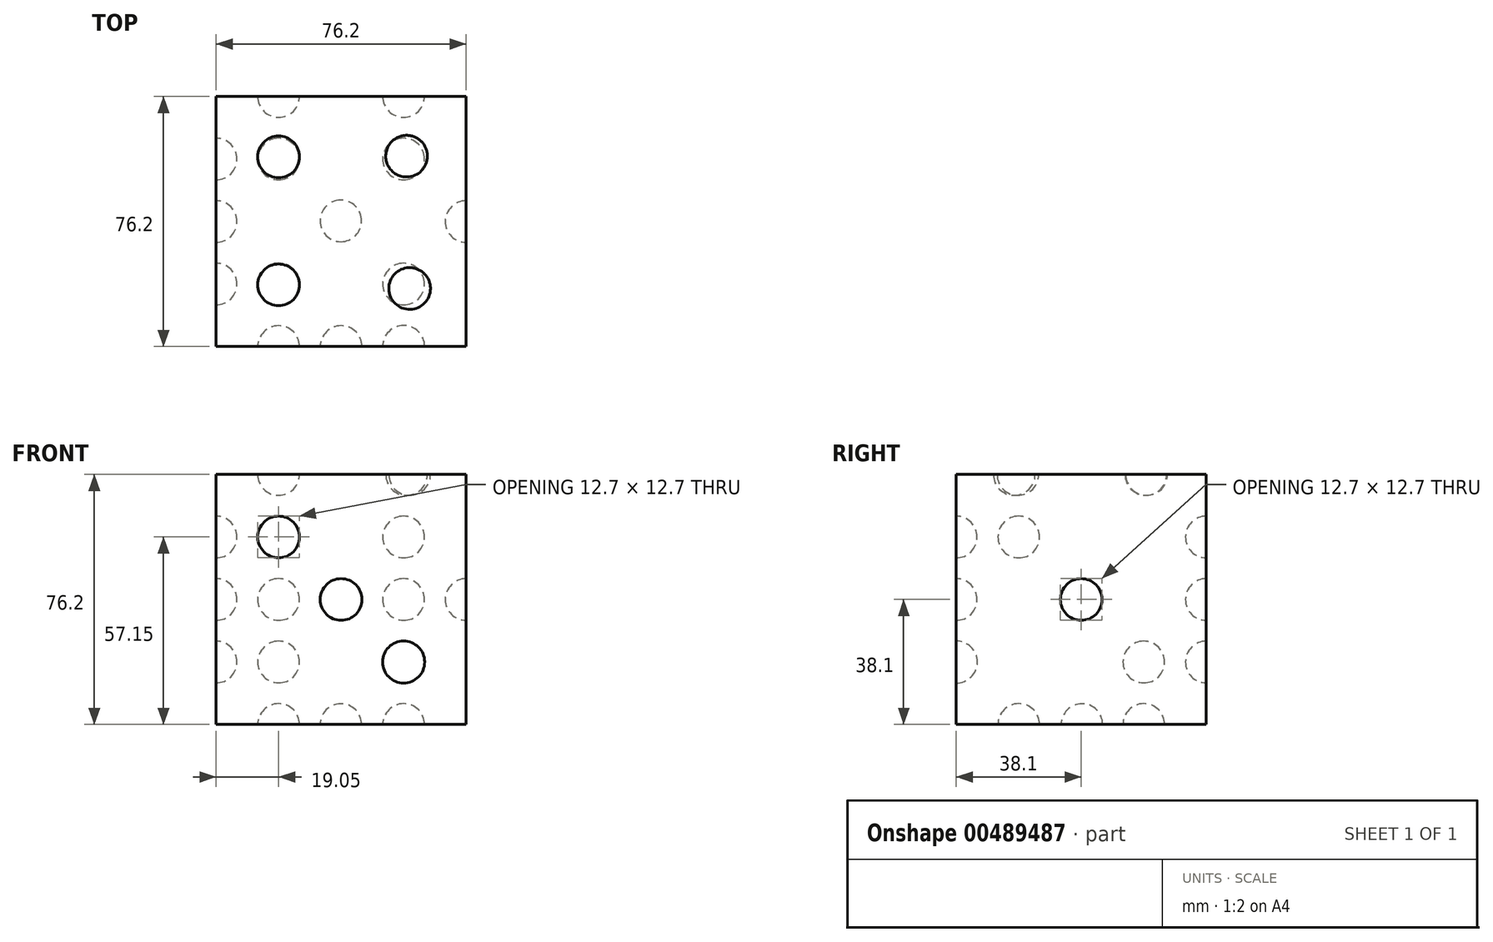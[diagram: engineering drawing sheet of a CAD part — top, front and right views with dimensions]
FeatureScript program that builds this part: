
annotation { "Feature Type Name" : "Feature", "Feature Type Description" : "" }
export const myFeature = defineFeature(function(context is Context, id is Id, definition is map)
    precondition{}
    {
        {
            var Q0;
            Q0=qCreatedBy(makeId("Front.planeOp"),FACE);
            var sketch = newSketch(context, id + "F0", { "sketchPlane" : qUnion([Q0])});
            skLineSegment(sketch, "E0.bottom", {"start": v(0, 76.2) * mm, "end": v(76.2, 76.2) * mm});
            skLineSegment(sketch, "E0.top", {"start": v(0, 0) * mm, "end": v(76.2, 0) * mm});
            skLineSegment(sketch, "E0.left", {"start": v(0, 76.2) * mm, "end": v(0, 0) * mm});
            skLineSegment(sketch, "E0.right", {"start": v(76.2, 76.2) * mm, "end": v(76.2, 0) * mm});
            skSolve(sketch);
        }
        {
            var Q0;
            Q0=makeQuery(id+"F0.imprint","IMPRINT",FACE,{"disambiguationData":[TD([[makeQuery(id+"F0.imprint","IMPRINT",EDGE,{"derivedFrom":sQuery(id+"F0.wireOp",EDGE,"E0.bottom")}),-1.0]])]});
            extrude(context, id + "F1", {"entities" : qUnion([Q0]), "depth" : 76.2 * mm});
        }
        {
            var Q0;
            Q0=makeQuery(id+"F1.opExtrude","SWEPT_FACE",FACE,{"disambiguationData":[OSD([sQuery(id+"F0.wireOp",EDGE,"E0.right")])]});
            var sketch = newSketch(context, id + "F2", { "sketchPlane" : qUnion([Q0])});
            skArc(sketch, "E1", {"start": v(-38.1, 44.45) * mm, "mid": v(-44.45, 38.1) * mm, "end": v(-38.1, 31.75) * mm});
            skLineSegment(sketch, "E2", {"start": v(-38.1, 38.1) * mm, "end": v(-38.1, 44.45) * mm});
            skPoint(sketch, "E3.orphan", {"position": v(-76.2, 0) * mm});
            skPoint(sketch, "E4.orphan", {"position": v(0, 76.2) * mm});
            skPoint(sketch, "E5.end.orphan", {"position": v(-38.1, 0) * mm});
            skPoint(sketch, "E6.orphan", {"position": v(-38.1, 76.2) * mm});
            skLineSegment(sketch, "E7", {"start": v(-38.1, 76.2) * mm, "end": v(-38.1, 0) * mm});
            skSolve(sketch);
        }
        {
            var Q0;
            {var subQ0=sQuery(id+"F2.wireOp",EDGE,"E1");Q0=makeQuery(id+"F2.imprint","IMPRINT",FACE,{"disambiguationData":[TD([[makeQuery(id+"F2.imprint","IMPRINT",EDGE,{"derivedFrom":subQ0}),1.0]])]});}
            var Q1;
            Q1=sQuery(id+"F2.wireOp",EDGE,"E7");
            revolve(context, id + "F3", {"operationType" : NewBodyOperationType.REMOVE, "entities" : qUnion([Q0]), "axis" : qUnion([Q1]), "revolveType" : RevolveType.FULL, "oppositeDirection" : true});
        }
        {
            var Q0;
            Q0=qCreatedBy(makeId("Top.planeOp"),FACE);
            var sketch = newSketch(context, id + "F4", { "sketchPlane" : qUnion([Q0])});
            skArc(sketch, "E8", {"start": v(38.01, -31.57) * mm, "mid": v(31.68, -37.9) * mm, "end": v(38.01, -44.23) * mm});
            skPoint(sketch, "E9.orphan", {"position": v(0, 0) * mm});
            skPoint(sketch, "E10.start.orphan", {"position": v(76.02, 0) * mm});
            skPoint(sketch, "E11.trimOffspring.end.orphan", {"position": v(0, -75.8) * mm});
            skPoint(sketch, "E12.end.orphan", {"position": v(76.02, -75.8) * mm});
            skLineSegment(sketch, "E13", {"start": v(38.01, -37.9) * mm, "end": v(38.01, 0) * mm});
            skLineSegment(sketch, "E14", {"start": v(38.01, -37.9) * mm, "end": v(38.01, -76.25) * mm});
            skLineSegment(sketch, "E15", {"start": v(38.01, 0) * mm, "end": v(38.01, -66.48) * mm});
            skLineSegment(sketch, "E16", {"start": v(38.01, -66.48) * mm, "end": v(38.01, 0) * mm});
            skSolve(sketch);
        }
        {
            var Q0;
            Q0 = qSketchRegion(id + "F4", true);
            var Q1;
            Q1=sQuery(id+"F4.wireOp",EDGE,"E16");
            revolve(context, id + "F5", {"operationType" : NewBodyOperationType.REMOVE, "entities" : qUnion([Q0]), "axis" : qUnion([Q1]), "revolveType" : RevolveType.FULL});
        }
        {
            var Q0;
            Q0=makeQuery(id+"F1.opExtrude","SWEPT_FACE",FACE,{"disambiguationData":[OSD([sQuery(id+"F0.wireOp",EDGE,"E0.bottom")])]});
            var sketch = newSketch(context, id + "F6", { "sketchPlane" : qUnion([Q0])});
            skSolve(sketch);
        }
        {
            var Q0;
            Q0=makeQuery(id+"F1.opExtrude","SWEPT_FACE",FACE,{"disambiguationData":[OSD([sQuery(id+"F0.wireOp",EDGE,"E0.top")])]});
            var sketch = newSketch(context, id + "F7", { "sketchPlane" : qUnion([Q0])});
            skArc(sketch, "E17", {"start": v(33.6, 33.6) * mm, "mid": v(43.97, 40.53) * mm, "end": v(31.75, 38.1) * mm});
            skPoint(sketch, "E18.orphan", {"position": v(38.1, 76.2) * mm});
            skPoint(sketch, "E19.orphan", {"position": v(38.1, 0) * mm});
            skLineSegment(sketch, "E20", {"start": v(19.05, 76.2) * mm, "end": v(19.05, 0) * mm});
            skPoint(sketch, "E20.startSnap0", {"position": v(19.05, 57.15) * mm});
            skPoint(sketch, "E21.startSnap0", {"position": v(57.15, 57.15) * mm});
            skPoint(sketch, "E22.orphan", {"position": v(0, 38.1) * mm});
            skPoint(sketch, "E23.end.orphan", {"position": v(76.2, 38.1) * mm});
            skArc(sketch, "E24", {"start": v(19.05, 63.5) * mm, "mid": v(12.7, 57.15) * mm, "end": v(19.05, 50.8) * mm});
            skArc(sketch, "E25", {"start": v(57.15, 63.5) * mm, "mid": v(50.8, 57.15) * mm, "end": v(57.15, 50.8) * mm});
            skPoint(sketch, "E26.orphan", {"position": v(57.15, 0) * mm});
            skPoint(sketch, "E21.start.orphan", {"position": v(57.15, 76.2) * mm});
            skSolve(sketch);
        }
        {
            var Q0;
            {var subQ1=sQuery(id+"F0.wireOp",EDGE,"E0.top");var subQ6=makeQuery(id+"F1.opExtrude","SWEPT_EDGE",EDGE,{"disambiguationData":[OSD([subQ1,sQuery(id+"F0.wireOp",EDGE,"E0.right")])]});Q0=makeQuery(id+"F7.imprint","IMPRINT",FACE,{"disambiguationData":[TD([[makeQuery(id+"F7.imprint","IMPRINT",EDGE,{"derivedFrom":subQ6}),-1.0]])]});}
            var sketch = newSketch(context, id + "F8", { "sketchPlane" : qUnion([Q0])});
            skSolve(sketch);
        }
        {
            var Q0;
            Q0 = qSketchRegion(id + "F7", true);
            var Q1;
            Q1=sQuery(id+"F7.wireOp",EDGE,"E20");
            revolve(context, id + "F9", {"operationType" : NewBodyOperationType.REMOVE, "entities" : qUnion([Q0]), "axis" : qUnion([Q1]), "revolveType" : RevolveType.FULL, "oppositeDirection" : true});
        }
        {
            var Q0;
            Q0=makeQuery(id+"F1.opExtrude","SWEPT_FACE",FACE,{"disambiguationData":[OSD([sQuery(id+"F0.wireOp",EDGE,"E0.top")])]});
            var sketch = newSketch(context, id + "F10", { "sketchPlane" : qUnion([Q0])});
            skLineSegment(sketch, "E27", {"start": v(57.15, 76.2) * mm, "end": v(57.15, 0) * mm});
            skPoint(sketch, "E27.startSnap0", {"position": v(57.15, 57.15) * mm});
            skPoint(sketch, "E28.orphan", {"position": v(38.1, 76.2) * mm});
            skPoint(sketch, "E29.end.orphan", {"position": v(76.2, 38.1) * mm});
            skArc(sketch, "E30", {"start": v(57.15, 63.5) * mm, "mid": v(50.8, 57.15) * mm, "end": v(57.15, 50.8) * mm});
            skSolve(sketch);
        }
        {
            var Q0;
            Q0 = qSketchRegion(id + "F10", true);
            var Q1;
            Q1=sQuery(id+"F10.wireOp",EDGE,"E27");
            revolve(context, id + "F11", {"operationType" : NewBodyOperationType.REMOVE, "entities" : qUnion([Q0]), "axis" : qUnion([Q1]), "revolveType" : RevolveType.FULL, "oppositeDirection" : true});
        }
        {
            var Q0;
            Q0=makeQuery(id+"F1.opExtrude","SWEPT_FACE",FACE,{"disambiguationData":[OSD([sQuery(id+"F0.wireOp",EDGE,"E0.top")])]});
            var sketch = newSketch(context, id + "F12", { "sketchPlane" : qUnion([Q0])});
            skLineSegment(sketch, "E31", {"start": v(57.15, 57.15) * mm, "end": v(57.15, 0) * mm});
            skArc(sketch, "E32", {"start": v(57.15, 25.4) * mm, "mid": v(50.8, 19.05) * mm, "end": v(57.15, 12.7) * mm});
            skPoint(sketch, "E33.orphan", {"position": v(76.2, 38.1) * mm});
            skPoint(sketch, "E34.orphan", {"position": v(38.1, 0) * mm});
            skSolve(sketch);
        }
        {
            var Q0;
            Q0 = qSketchRegion(id + "F12", true);
            var Q1;
            Q1=sQuery(id+"F12.wireOp",EDGE,"E31");
            revolve(context, id + "F13", {"operationType" : NewBodyOperationType.REMOVE, "entities" : qUnion([Q0]), "axis" : qUnion([Q1]), "revolveType" : RevolveType.FULL, "oppositeDirection" : true});
        }
        {
            var Q0;
            Q0=makeQuery(id+"F1.opExtrude","SWEPT_FACE",FACE,{"disambiguationData":[OSD([sQuery(id+"F0.wireOp",EDGE,"E0.top")])]});
            var sketch = newSketch(context, id + "F14", { "sketchPlane" : qUnion([Q0])});
            skLineSegment(sketch, "E35", {"start": v(19.05, 57.15) * mm, "end": v(19.05, 0) * mm});
            skArc(sketch, "E36", {"start": v(19.05, 25.4) * mm, "mid": v(12.7, 19.05) * mm, "end": v(19.05, 12.7) * mm});
            skPoint(sketch, "E36.perimeterSnap0", {"position": v(19.05, 19.05) * mm});
            skPoint(sketch, "E37.orphan", {"position": v(0, 38.1) * mm});
            skPoint(sketch, "E38.orphan", {"position": v(38.1, 0) * mm});
            skSolve(sketch);
        }
        {
            var Q0;
            Q0 = qSketchRegion(id + "F14", true);
            var Q1;
            Q1=sQuery(id+"F14.wireOp",EDGE,"E35");
            revolve(context, id + "F15", {"operationType" : NewBodyOperationType.REMOVE, "entities" : qUnion([Q0]), "axis" : qUnion([Q1]), "revolveType" : RevolveType.FULL, "oppositeDirection" : true});
        }
        {
            var Q0;
            Q0=makeQuery(id+"F1.opExtrude","CAP_FACE",FACE,{"disambiguationData":[OSD([sQuery(id+"F0.wireOp",EDGE,"E0.bottom"),sQuery(id+"F0.wireOp",EDGE,"E0.top"),sQuery(id+"F0.wireOp",EDGE,"E0.left"),sQuery(id+"F0.wireOp",EDGE,"E0.right")])],"isStart":false});
            var sketch = newSketch(context, id + "F16", { "sketchPlane" : qUnion([Q0])});
            skArc(sketch, "E39", {"start": v(19.05, 63.5) * mm, "mid": v(12.7, 57.15) * mm, "end": v(19.05, 50.8) * mm});
            skArc(sketch, "E40", {"start": v(38.1, 44.45) * mm, "mid": v(31.75, 38.1) * mm, "end": v(38.1, 31.75) * mm});
            skArc(sketch, "E41", {"start": v(57.15, 25.4) * mm, "mid": v(50.8, 19.05) * mm, "end": v(57.15, 12.7) * mm});
            skLineSegment(sketch, "E42", {"start": v(19.05, 76.2) * mm, "end": v(19.05, 0) * mm});
            skPoint(sketch, "E43.orphan", {"position": v(0, 38.1) * mm});
            skPoint(sketch, "E44.start.orphan", {"position": v(0, 0) * mm});
            skPoint(sketch, "E45.trimOffspring.end.orphan", {"position": v(76.2, 76.2) * mm});
            skPoint(sketch, "E46.orphan", {"position": v(76.2, 38.1) * mm});
            skPoint(sketch, "E47.orphan", {"position": v(38.1, 0) * mm});
            skPoint(sketch, "E48.orphan", {"position": v(38.1, 76.2) * mm});
            skPoint(sketch, "E49.orphan", {"position": v(57.15, 76.2) * mm});
            skPoint(sketch, "E50.end.orphan", {"position": v(57.15, 0) * mm});
            skSolve(sketch);
        }
        {
            var Q0;
            Q0 = qSketchRegion(id + "F16", true);
            var Q1;
            Q1=sQuery(id+"F16.wireOp",EDGE,"E42");
            revolve(context, id + "F17", {"operationType" : NewBodyOperationType.REMOVE, "entities" : qUnion([Q0]), "axis" : qUnion([Q1]), "revolveType" : RevolveType.FULL, "oppositeDirection" : true});
        }
        {
            var Q0;
            Q0=makeQuery(id+"F1.opExtrude","CAP_FACE",FACE,{"disambiguationData":[OSD([sQuery(id+"F0.wireOp",EDGE,"E0.bottom"),sQuery(id+"F0.wireOp",EDGE,"E0.top"),sQuery(id+"F0.wireOp",EDGE,"E0.left"),sQuery(id+"F0.wireOp",EDGE,"E0.right")])],"isStart":false});
            var sketch = newSketch(context, id + "F18", { "sketchPlane" : qUnion([Q0])});
            skPoint(sketch, "E51.startSnap0", {"position": v(57.15, 57.15) * mm});
            skPoint(sketch, "E52.orphan", {"position": v(38.1, 76.2) * mm});
            skPoint(sketch, "E53.orphan", {"position": v(76.2, 38.1) * mm});
            skPoint(sketch, "E51.start.orphan", {"position": v(57.15, 76.2) * mm});
            skLineSegment(sketch, "E54", {"start": v(38.1, 76.2) * mm, "end": v(38.1, 0) * mm});
            skArc(sketch, "E55", {"start": v(38.1, 44.45) * mm, "mid": v(31.75, 38.1) * mm, "end": v(38.1, 31.75) * mm});
            skPoint(sketch, "E56.orphan", {"position": v(0, 38.1) * mm});
            skSolve(sketch);
        }
        {
            var Q0;
            Q0 = qSketchRegion(id + "F18", true);
            var Q1;
            Q1=sQuery(id+"F18.wireOp",EDGE,"E54");
            revolve(context, id + "F19", {"operationType" : NewBodyOperationType.REMOVE, "entities" : qUnion([Q0]), "axis" : qUnion([Q1]), "revolveType" : RevolveType.FULL, "oppositeDirection" : true});
        }
        {
            var Q0;
            Q0=makeQuery(id+"F1.opExtrude","CAP_FACE",FACE,{"disambiguationData":[OSD([sQuery(id+"F0.wireOp",EDGE,"E0.bottom"),sQuery(id+"F0.wireOp",EDGE,"E0.top"),sQuery(id+"F0.wireOp",EDGE,"E0.left"),sQuery(id+"F0.wireOp",EDGE,"E0.right")])],"isStart":false});
            var sketch = newSketch(context, id + "F20", { "sketchPlane" : qUnion([Q0])});
            skLineSegment(sketch, "E57", {"start": v(57.15, 0) * mm, "end": v(57.15, 76.2) * mm});
            skPoint(sketch, "E57.startSnap0", {"position": v(57.15, 19.05) * mm});
            skArc(sketch, "E58", {"start": v(57.15, 25.46) * mm, "mid": v(50.74, 19.05) * mm, "end": v(57.15, 12.64) * mm});
            skPoint(sketch, "E59.orphan", {"position": v(76.2, 38.1) * mm});
            skPoint(sketch, "E60.orphan", {"position": v(38.1, 0) * mm});
            skSolve(sketch);
        }
        {
            var Q0;
            Q0 = qSketchRegion(id + "F20", true);
            var Q1;
            Q1=sQuery(id+"F20.wireOp",EDGE,"E57");
            revolve(context, id + "F21", {"operationType" : NewBodyOperationType.REMOVE, "entities" : qUnion([Q0]), "axis" : qUnion([Q1]), "revolveType" : RevolveType.FULL, "oppositeDirection" : true});
        }
        {
            var Q0;
            {var subQ0=sQuery(id+"F0.wireOp",EDGE,"E0.bottom");Q0=makeQuery(id+"F6.imprint","IMPRINT",FACE,{"disambiguationData":[TD([[makeQuery(id+"F6.imprint","IMPRINT",EDGE,{"derivedFrom":makeQuery(id+"F1.opExtrude","CAP_EDGE",EDGE,{"disambiguationData":[OSD([subQ0])],"isStart":true})}),-1.0]])]});}
            var sketch = newSketch(context, id + "F22", { "sketchPlane" : qUnion([Q0])});
            skLineSegment(sketch, "E61", {"start": v(0, 0) * mm, "end": v(38.1, 0) * mm});
            skLineSegment(sketch, "E62", {"start": v(19.05, 0) * mm, "end": v(19.05, -76.9) * mm});
            skArc(sketch, "E63", {"start": v(19.05, -12.05) * mm, "mid": v(12.7, -18.4) * mm, "end": v(19.05, -24.75) * mm});
            skArc(sketch, "E64", {"start": v(19.05, -51.05) * mm, "mid": v(12.7, -57.4) * mm, "end": v(19.05, -63.75) * mm});
            skLineSegment(sketch, "E65", {"start": v(38.1, 0) * mm, "end": v(75.8, 0) * mm});
            skLineSegment(sketch, "E66", {"start": v(56.95, 0) * mm, "end": v(56.95, -76.46) * mm});
            skPoint(sketch, "E67.start.orphan", {"position": v(0, -39) * mm});
            skSolve(sketch);
        }
        {
            var Q0;
            Q0 = qSketchRegion(id + "F22", true);
            var Q1;
            Q1=sQuery(id+"F22.wireOp",EDGE,"E62");
            revolve(context, id + "F23", {"operationType" : NewBodyOperationType.REMOVE, "entities" : qUnion([Q0]), "axis" : qUnion([Q1]), "revolveType" : RevolveType.FULL, "oppositeDirection" : true});
        }
        {
            var Q0;
            {var subQ0=sQuery(id+"F0.wireOp",EDGE,"E0.bottom");Q0=makeQuery(id+"F6.imprint","IMPRINT",FACE,{"disambiguationData":[TD([[makeQuery(id+"F6.imprint","IMPRINT",EDGE,{"derivedFrom":makeQuery(id+"F1.opExtrude","CAP_EDGE",EDGE,{"disambiguationData":[OSD([subQ0])],"isStart":true})}),-1.0]])]});}
            var sketch = newSketch(context, id + "F24", { "sketchPlane" : qUnion([Q0])});
            skLineSegment(sketch, "E68", {"start": v(0, 0) * mm, "end": v(38.12, 0) * mm});
            skLineSegment(sketch, "E69", {"start": v(57.62, 0) * mm, "end": v(59.4, -76.69) * mm});
            skArc(sketch, "E70", {"start": v(57.9, -11.83) * mm, "mid": v(51.7, -18.32) * mm, "end": v(58.2, -24.52) * mm});
            skArc(sketch, "E71", {"start": v(58.83, -52.16) * mm, "mid": v(52.63, -58.66) * mm, "end": v(59.12, -64.86) * mm});
            skPoint(sketch, "E72.orphan", {"position": v(0, -18.17) * mm});
            skPoint(sketch, "E73.end.orphan", {"position": v(39.9, -76.69) * mm});
            skPoint(sketch, "E74.orphan", {"position": v(0, -58.51) * mm});
            skPoint(sketch, "E75.end.orphan", {"position": v(76.24, -58.51) * mm});
            skPoint(sketch, "E76.orphan", {"position": v(76.24, -18.17) * mm});
            skSolve(sketch);
        }
        {
            var Q0;
            Q0 = qSketchRegion(id + "F24", true);
            var Q1;
            Q1=sQuery(id+"F24.wireOp",EDGE,"E69");
            revolve(context, id + "F25", {"operationType" : NewBodyOperationType.REMOVE, "entities" : qUnion([Q0]), "axis" : qUnion([Q1]), "revolveType" : RevolveType.FULL, "oppositeDirection" : true});
        }
        {
            var Q0;
            Q0=makeQuery(id+"F1.opExtrude","CAP_FACE",FACE,{"disambiguationData":[OSD([sQuery(id+"F0.wireOp",EDGE,"E0.bottom"),sQuery(id+"F0.wireOp",EDGE,"E0.top"),sQuery(id+"F0.wireOp",EDGE,"E0.left"),sQuery(id+"F0.wireOp",EDGE,"E0.right")])],"isStart":true});
            var sketch = newSketch(context, id + "F26", { "sketchPlane" : qUnion([Q0])});
            skLineSegment(sketch, "E77", {"start": v(-76.2, 76.2) * mm, "end": v(-38.1, 76.2) * mm});
            skLineSegment(sketch, "E78", {"start": v(-57.15, 76.2) * mm, "end": v(-57.15, 0) * mm});
            skLineSegment(sketch, "E79", {"start": v(-38.1, 76.2) * mm, "end": v(0, 76.2) * mm});
            skArc(sketch, "E80", {"start": v(-57.15, 63.5) * mm, "mid": v(-63.5, 57.15) * mm, "end": v(-57.15, 50.8) * mm});
            skArc(sketch, "E81", {"start": v(-57.15, 44.45) * mm, "mid": v(-63.5, 38.1) * mm, "end": v(-57.15, 31.75) * mm});
            skArc(sketch, "E82", {"start": v(-57.15, 25.4) * mm, "mid": v(-63.5, 19.05) * mm, "end": v(-57.15, 12.7) * mm});
            skArc(sketch, "E83", {"start": v(-19.05, 63.5) * mm, "mid": v(-25.4, 57.15) * mm, "end": v(-19.05, 50.8) * mm});
            skArc(sketch, "E84", {"start": v(-19.05, 25.4) * mm, "mid": v(-25.4, 19.05) * mm, "end": v(-19.05, 12.7) * mm});
            skPoint(sketch, "E85.orphan", {"position": v(-76.2, 38.1) * mm});
            skPoint(sketch, "E86.orphan", {"position": v(0, 38.1) * mm});
            skPoint(sketch, "E87.orphan", {"position": v(-38.1, 0) * mm});
            skPoint(sketch, "E88.trimOffspring.end.orphan", {"position": v(-19.05, 38.1) * mm});
            skArc(sketch, "E89", {"start": v(-19.05, 44.45) * mm, "mid": v(-25.4, 38.1) * mm, "end": v(-19.05, 31.75) * mm});
            skPoint(sketch, "E90.orphan", {"position": v(-19.05, 76.2) * mm});
            skPoint(sketch, "E91.orphan", {"position": v(-19.05, 0) * mm});
            skSolve(sketch);
        }
        {
            var Q0;
            Q0 = qSketchRegion(id + "F26", true);
            var Q1;
            Q1=sQuery(id+"F26.wireOp",EDGE,"E78");
            revolve(context, id + "F27", {"operationType" : NewBodyOperationType.REMOVE, "entities" : qUnion([Q0]), "axis" : qUnion([Q1]), "revolveType" : RevolveType.FULL});
        }
        {
            var Q0;
            Q0=makeQuery(id+"F1.opExtrude","CAP_FACE",FACE,{"disambiguationData":[OSD([sQuery(id+"F0.wireOp",EDGE,"E0.bottom"),sQuery(id+"F0.wireOp",EDGE,"E0.top"),sQuery(id+"F0.wireOp",EDGE,"E0.left"),sQuery(id+"F0.wireOp",EDGE,"E0.right")])],"isStart":true});
            var sketch = newSketch(context, id + "F28", { "sketchPlane" : qUnion([Q0])});
            skLineSegment(sketch, "E92", {"start": v(-19.05, 76.2) * mm, "end": v(-19.05, 0) * mm});
            skPoint(sketch, "E92.startSnap0", {"position": v(-19.05, 57.15) * mm});
            skArc(sketch, "E93", {"start": v(-19.05, 63.5) * mm, "mid": v(-25.4, 57.15) * mm, "end": v(-19.05, 50.8) * mm});
            skArc(sketch, "E94", {"start": v(-19.05, 44.45) * mm, "mid": v(-25.4, 38.1) * mm, "end": v(-19.05, 31.75) * mm});
            skArc(sketch, "E95", {"start": v(-19.05, 25.4) * mm, "mid": v(-25.4, 19.05) * mm, "end": v(-19.05, 12.7) * mm});
            skPoint(sketch, "E96.orphan", {"position": v(-38.1, 38.1) * mm});
            skPoint(sketch, "E97.start.orphan", {"position": v(-38.1, 76.2) * mm});
            skPoint(sketch, "E98.orphan", {"position": v(0, 38.1) * mm});
            skPoint(sketch, "E99.end.orphan", {"position": v(-38.1, 0) * mm});
            skSolve(sketch);
        }
        {
            var Q0;
            Q0 = qSketchRegion(id + "F28", true);
            var Q1;
            Q1=sQuery(id+"F28.wireOp",EDGE,"E92");
            revolve(context, id + "F29", {"operationType" : NewBodyOperationType.REMOVE, "entities" : qUnion([Q0]), "axis" : qUnion([Q1]), "revolveType" : RevolveType.FULL, "oppositeDirection" : true});
        }
        {
            var Q0;
            Q0=makeQuery(id+"F1.opExtrude","SWEPT_FACE",FACE,{"disambiguationData":[OSD([sQuery(id+"F0.wireOp",EDGE,"E0.left")])]});
            var sketch = newSketch(context, id + "F30", { "sketchPlane" : qUnion([Q0])});
            skLineSegment(sketch, "E100", {"start": v(38.1, 44.45) * mm, "end": v(38.1, 38.1) * mm});
            skLineSegment(sketch, "E101", {"start": v(19.05, 19.05) * mm, "end": v(19.05, 25.4) * mm});
            skPoint(sketch, "E101.startSnap0", {"position": v(19.05, 19.05) * mm});
            skLineSegment(sketch, "E102", {"start": v(57.15, 63.5) * mm, "end": v(57.15, 57.15) * mm});
            skPoint(sketch, "E102.startSnap0", {"position": v(57.15, 57.15) * mm});
            skArc(sketch, "E103", {"start": v(19.05, 25.4) * mm, "mid": v(12.7, 19.05) * mm, "end": v(19.05, 12.7) * mm});
            skArc(sketch, "E104", {"start": v(38.1, 44.45) * mm, "mid": v(31.75, 38.1) * mm, "end": v(38.1, 31.75) * mm});
            skArc(sketch, "E105", {"start": v(57.15, 63.5) * mm, "mid": v(50.8, 57.15) * mm, "end": v(57.15, 50.8) * mm});
            skPoint(sketch, "E106.orphan", {"position": v(0, 0) * mm});
            skPoint(sketch, "E107.orphan", {"position": v(76.2, 76.2) * mm});
            skPoint(sketch, "E108.orphan", {"position": v(38.1, 76.2) * mm});
            skPoint(sketch, "E109.orphan", {"position": v(57.15, 76.2) * mm});
            skLineSegment(sketch, "E110.trimOffspring", {"start": v(38.1, 31.75) * mm, "end": v(38.1, 0) * mm});
            skLineSegment(sketch, "E111.trimOffspring", {"start": v(57.15, 50.8) * mm, "end": v(57.15, 0) * mm});
            skPoint(sketch, "E112.orphan", {"position": v(19.05, 0) * mm});
            skLineSegment(sketch, "E113", {"start": v(38.1, 31.75) * mm, "end": v(38.1, 76.2) * mm});
            skLineSegment(sketch, "E114", {"start": v(57.15, 57.15) * mm, "end": v(57.15, 76.2) * mm});
            skSolve(sketch);
        }
        {
            var Q0;
            Q0 = qSketchRegion(id + "F30", true);
            var Q1;
            Q1=sQuery(id+"F30.wireOp",EDGE,"E113");
            revolve(context, id + "F31", {"operationType" : NewBodyOperationType.REMOVE, "entities" : qUnion([Q0]), "axis" : qUnion([Q1]), "revolveType" : RevolveType.FULL, "oppositeDirection" : true});
        }
        {
            var Q0;
            Q0=makeQuery(id+"F1.opExtrude","SWEPT_FACE",FACE,{"disambiguationData":[OSD([sQuery(id+"F0.wireOp",EDGE,"E0.left")])]});
            var sketch = newSketch(context, id + "F32", { "sketchPlane" : qUnion([Q0])});
            skLineSegment(sketch, "E115", {"start": v(19.05, 0) * mm, "end": v(19.05, 76.2) * mm});
            skPoint(sketch, "E115.startSnap0", {"position": v(19.05, 19.05) * mm});
            skLineSegment(sketch, "E116", {"start": v(38.1, 76.2) * mm, "end": v(76.2, 38.1) * mm});
            skLineSegment(sketch, "E117", {"start": v(57.15, 76.2) * mm, "end": v(57.15, 0) * mm});
            skPoint(sketch, "E117.startSnap0", {"position": v(57.15, 57.15) * mm});
            skArc(sketch, "E118", {"start": v(19.05, 25.4) * mm, "mid": v(12.7, 19.05) * mm, "end": v(19.05, 12.7) * mm});
            skPoint(sketch, "E119.orphan", {"position": v(0, 38.1) * mm});
            skPoint(sketch, "E120.end.orphan", {"position": v(38.1, 0) * mm});
            skSolve(sketch);
        }
        {
            var Q0;
            Q0 = qSketchRegion(id + "F32", true);
            var Q1;
            Q1=sQuery(id+"F32.wireOp",EDGE,"E115");
            revolve(context, id + "F33", {"operationType" : NewBodyOperationType.REMOVE, "entities" : qUnion([Q0]), "axis" : qUnion([Q1]), "revolveType" : RevolveType.FULL, "oppositeDirection" : true});
        }
        {
            var Q0;
            Q0=makeQuery(id+"F1.opExtrude","SWEPT_FACE",FACE,{"disambiguationData":[OSD([sQuery(id+"F0.wireOp",EDGE,"E0.left")])]});
            var sketch = newSketch(context, id + "F34", { "sketchPlane" : qUnion([Q0])});
            skLineSegment(sketch, "E121", {"start": v(57.15, 76.2) * mm, "end": v(57.15, 0) * mm});
            skPoint(sketch, "E121.startSnap0", {"position": v(57.15, 57.15) * mm});
            skArc(sketch, "E122", {"start": v(57.15, 63.5) * mm, "mid": v(50.8, 57.15) * mm, "end": v(57.15, 50.8) * mm});
            skPoint(sketch, "E123.orphan", {"position": v(38.1, 76.2) * mm});
            skPoint(sketch, "E124.orphan", {"position": v(76.2, 38.1) * mm});
            skSolve(sketch);
        }
        {
            var Q0;
            Q0 = qSketchRegion(id + "F34", true);
            var Q1;
            Q1=sQuery(id+"F34.wireOp",EDGE,"E121");
            revolve(context, id + "F35", {"operationType" : NewBodyOperationType.REMOVE, "entities" : qUnion([Q0]), "axis" : qUnion([Q1]), "revolveType" : RevolveType.FULL, "oppositeDirection" : true});
        }
    });
